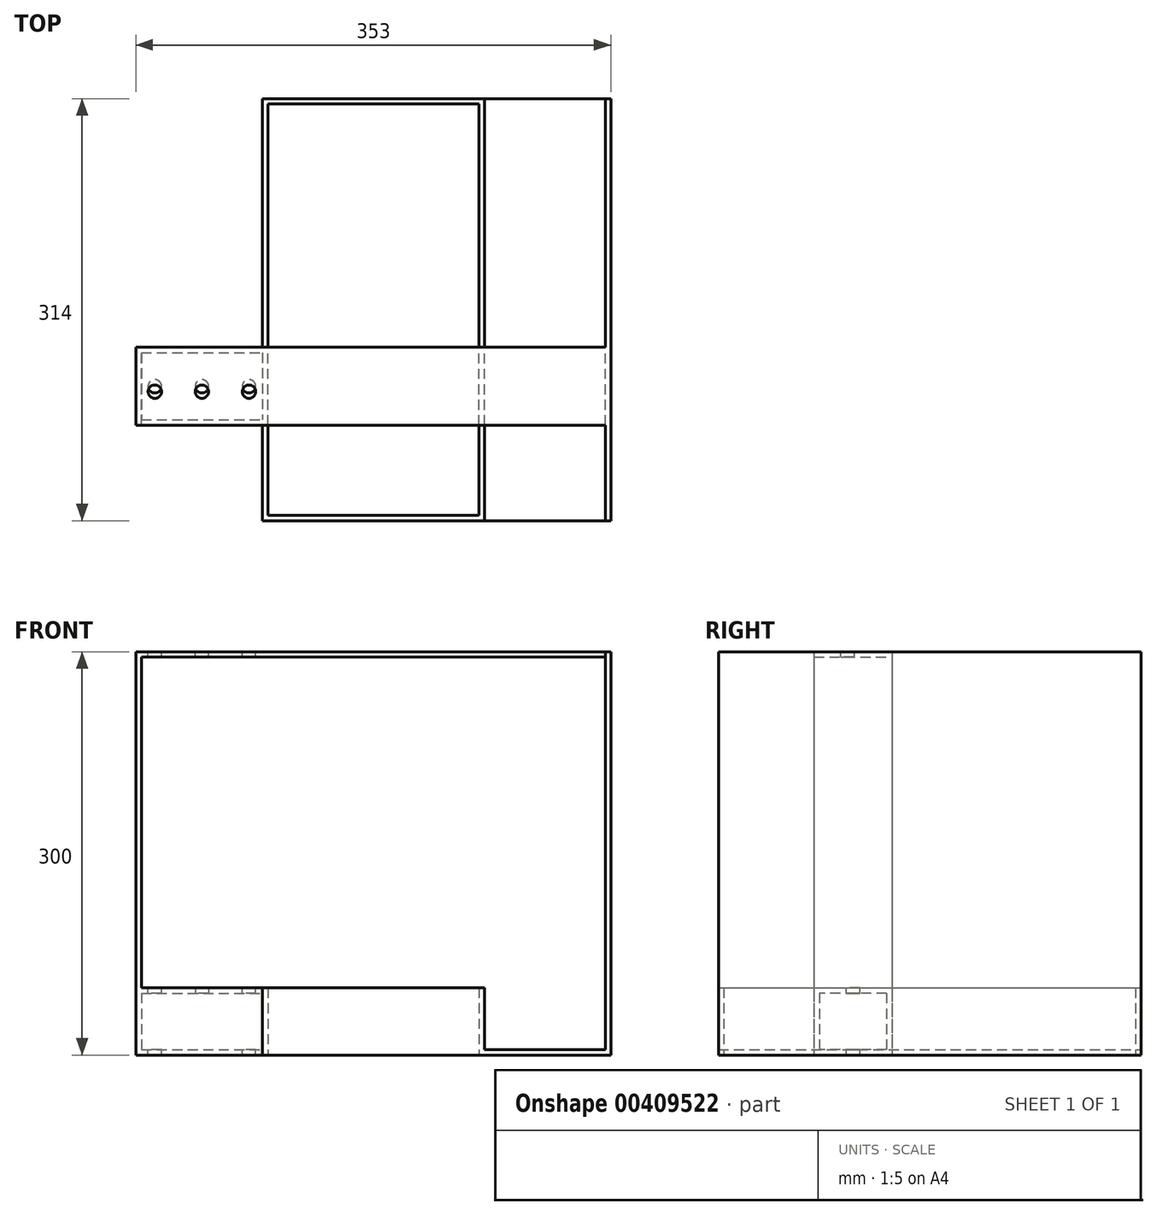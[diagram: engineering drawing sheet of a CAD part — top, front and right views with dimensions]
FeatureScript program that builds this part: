
annotation { "Feature Type Name" : "Feature", "Feature Type Description" : "" }
export const myFeature = defineFeature(function(context is Context, id is Id, definition is map)
    precondition{}
    {
        {
            var Q0;
            Q0=qCreatedBy(makeId("Top.planeOp"),FACE);
            var sketch = newSketch(context, id + "F0", { "sketchPlane" : qUnion([Q0])});
            skLineSegment(sketch, "E0.bottom", {"start": v(-82.5, -165.03) * mm, "end": v(82.5, -165.03) * mm});
            skLineSegment(sketch, "E0.top", {"start": v(-82.5, 148.97) * mm, "end": v(82.5, 148.97) * mm});
            skLineSegment(sketch, "E0.left", {"start": v(-82.5, -165.03) * mm, "end": v(-82.5, 148.97) * mm});
            skLineSegment(sketch, "E0.right", {"start": v(82.5, -165.03) * mm, "end": v(82.5, 148.97) * mm});
            skLineSegment(sketch, "E1.bottom", {"start": v(-78.5, -161.03) * mm, "end": v(78.5, -161.03) * mm});
            skLineSegment(sketch, "E1.top", {"start": v(-78.5, 144.97) * mm, "end": v(78.5, 144.97) * mm});
            skLineSegment(sketch, "E1.left", {"start": v(-78.5, -161.03) * mm, "end": v(-78.5, 144.97) * mm});
            skLineSegment(sketch, "E1.right", {"start": v(78.5, -161.03) * mm, "end": v(78.5, 144.97) * mm});
            skSolve(sketch);
        }
        {
            var Q0;
            Q0=makeQuery(id+"F0.imprint","IMPRINT",FACE,{"disambiguationData":[TD([[makeQuery(id+"F0.imprint","IMPRINT",EDGE,{"derivedFrom":sQuery(id+"F0.wireOp",EDGE,"E0.bottom")}),1.0]])]});
            extrude(context, id + "F1", {"entities" : qUnion([Q0]), "depth" : 50 * mm});
        }
        {
            var Q0;
            Q0=makeQuery(id+"F1.opExtrude","SWEPT_FACE",FACE,{"disambiguationData":[OSD([sQuery(id+"F0.wireOp",EDGE,"E0.left")])]});
            var sketch = newSketch(context, id + "F2", { "sketchPlane" : qUnion([Q0])});
            skLineSegment(sketch, "E2", {"start": v(65.03, 0) * mm, "end": v(65.03, 50) * mm});
            skLineSegment(sketch, "E3.bottom", {"start": v(36.03, 50) * mm, "end": v(94.03, 50) * mm});
            skLineSegment(sketch, "E3.top", {"start": v(36.03, 0) * mm, "end": v(94.03, 0) * mm});
            skLineSegment(sketch, "E3.left", {"start": v(36.03, 50) * mm, "end": v(36.03, 0) * mm});
            skLineSegment(sketch, "E3.right", {"start": v(94.03, 50) * mm, "end": v(94.03, 0) * mm});
            skLineSegment(sketch, "E4.bottom", {"start": v(40.03, 46) * mm, "end": v(90.03, 46) * mm});
            skLineSegment(sketch, "E4.top", {"start": v(40.03, 4) * mm, "end": v(90.03, 4) * mm});
            skLineSegment(sketch, "E4.left", {"start": v(40.03, 46) * mm, "end": v(40.03, 4) * mm});
            skLineSegment(sketch, "E4.right", {"start": v(90.03, 46) * mm, "end": v(90.03, 4) * mm});
            skSolve(sketch);
        }
        {
            var Q0;
            {var subQ3=sQuery(id+"F2.wireOp",EDGE,"E3.left");Q0=makeQuery(id+"F2.imprint","IMPRINT",FACE,{"disambiguationData":[TD([[makeQuery(id+"F2.imprint","IMPRINT",EDGE,{"derivedFrom":subQ3}),1.0]])]});}
            var Q1;
            {var subQ3=sQuery(id+"F2.wireOp",EDGE,"E3.right");Q1=makeQuery(id+"F2.imprint","IMPRINT",FACE,{"disambiguationData":[TD([[makeQuery(id+"F2.imprint","IMPRINT",EDGE,{"derivedFrom":subQ3}),-1.0]])]});}
            extrude(context, id + "F3", {"entities" : qUnion([Q0, Q1]), "operationType" : NewBodyOperationType.ADD, "depth" : 90 * mm});
        }
        {
            var Q0;
            Q0=makeQuery(id+"F3.opExtrude","SWEPT_FACE",FACE,{"disambiguationData":[OSD([sQuery(id+"F2.wireOp",EDGE,"E4.top")])]});
            var sketch = newSketch(context, id + "F4", { "sketchPlane" : qUnion([Q0])});
            skLineSegment(sketch, "E5.bottom", {"start": v(-172.5, 16.97) * mm, "end": v(-150.47, 16.97) * mm});
            skLineSegment(sketch, "E5.top", {"start": v(-172.5, -90.03) * mm, "end": v(-168.5, -90.03) * mm});
            skCircle(sketch, "E6", {"center": v(-92.5, -65.03) * mm, "radius": 5 * mm});
            skCircle(sketch, "E7", {"center": v(-162.5, -65.03) * mm, "radius": 5 * mm});
            skLineSegment(sketch, "E8.bottom", {"start": v(-102.5, -40.03) * mm, "end": v(-152.5, -40.03) * mm});
            skLineSegment(sketch, "E8.top", {"start": v(-102.5, -90.03) * mm, "end": v(-152.5, -90.03) * mm});
            skLineSegment(sketch, "E8.left", {"start": v(-102.5, -40.03) * mm, "end": v(-102.5, -90.03) * mm});
            skLineSegment(sketch, "E8.right", {"start": v(-152.5, -40.03) * mm, "end": v(-152.5, -90.03) * mm});
            skCircle(sketch, "E9", {"center": v(-127.5, -65.03) * mm, "radius": 5 * mm});
            skSolve(sketch);
        }
        {
            var Q0;
            Q0=makeQuery(id+"F4.imprint","IMPRINT",FACE,{"disambiguationData":[TD([[makeQuery(id+"F4.imprint","IMPRINT",EDGE,{"derivedFrom":sQuery(id+"F4.wireOp",EDGE,"E6")}),1.0]])]});
            var Q1;
            Q1=makeQuery(id+"F4.imprint","IMPRINT",FACE,{"disambiguationData":[TD([[makeQuery(id+"F4.imprint","IMPRINT",EDGE,{"derivedFrom":sQuery(id+"F4.wireOp",EDGE,"E7")}),1.0]])]});
            extrude(context, id + "F5", {"entities" : qUnion([Q0, Q1]), "operationType" : NewBodyOperationType.REMOVE, "oppositeDirection" : true, "depth" : 14 * mm, "hasSecondDirection" : true, "secondDirectionOppositeDirection" : false, "secondDirectionDepth" : 70 * mm});
        }
        {
            var Q0;
            Q0=makeQuery(id+"F4.imprint","IMPRINT",FACE,{"disambiguationData":[TD([[makeQuery(id+"F4.imprint","IMPRINT",EDGE,{"derivedFrom":sQuery(id+"F4.wireOp",EDGE,"E9")}),1.0]])]});
            extrude(context, id + "F6", {"entities" : qUnion([Q0]), "operationType" : NewBodyOperationType.REMOVE, "depth" : 50 * mm});
        }
        {
            var Q0;
            Q0=makeQuery(id+"F3.boolean.opBoolean","MERGE",FACE,{"derivedFrom":[makeQuery(id+"F1.opExtrude","CAP_FACE",FACE,{"disambiguationData":[OSD([sQuery(id+"F0.wireOp",EDGE,"E0.bottom"),sQuery(id+"F0.wireOp",EDGE,"E0.top"),sQuery(id+"F0.wireOp",EDGE,"E0.left"),sQuery(id+"F0.wireOp",EDGE,"E0.right"),sQuery(id+"F0.wireOp",EDGE,"E1.bottom"),sQuery(id+"F0.wireOp",EDGE,"E1.top"),sQuery(id+"F0.wireOp",EDGE,"E1.left"),sQuery(id+"F0.wireOp",EDGE,"E1.right")])],"isStart":true}),makeQuery(id+"F3.opExtrude","SWEPT_FACE",FACE,{"disambiguationData":[OSD([sQuery(id+"F2.wireOp",EDGE,"E3.top")])]})]});
            var sketch = newSketch(context, id + "F7", { "sketchPlane" : qUnion([Q0])});
            skLineSegment(sketch, "E10.bottom", {"start": v(-172.5, 36.03) * mm, "end": v(-176.5, 36.03) * mm});
            skLineSegment(sketch, "E10.top", {"start": v(-172.5, 94.03) * mm, "end": v(-176.5, 94.03) * mm});
            skLineSegment(sketch, "E10.left", {"start": v(-172.5, 36.03) * mm, "end": v(-172.5, 94.03) * mm});
            skLineSegment(sketch, "E10.right", {"start": v(-176.5, 36.03) * mm, "end": v(-176.5, 94.03) * mm});
            skSolve(sketch);
        }
        {
            var Q0;
            Q0 = qSketchRegion(id + "F7", true);
            extrude(context, id + "F8", {"entities" : qUnion([Q0]), "operationType" : NewBodyOperationType.ADD, "oppositeDirection" : true, "depth" : 300 * mm});
        }
        {
            var Q0;
            {var subQ1=sQuery(id+"F7.wireOp",EDGE,"E10.left");Q0=makeQuery(id+"F8.boolean.opBoolean","SPLIT",FACE,{"disambiguationData":[TD([makeQuery(id+"F3.opExtrude","SWEPT_FACE",FACE,{"disambiguationData":[OSD([sQuery(id+"F2.wireOp",EDGE,"E3.bottom")])]})])],"derivedFrom":makeQuery(id+"F8.opExtrude","SWEPT_FACE",FACE,{"disambiguationData":[OSD([subQ1])]})});}
            var sketch = newSketch(context, id + "F9", { "sketchPlane" : qUnion([Q0])});
            skLineSegment(sketch, "E11.bottom", {"start": v(-94.03, 300) * mm, "end": v(-36.03, 300) * mm});
            skLineSegment(sketch, "E11.top", {"start": v(-94.03, 296) * mm, "end": v(-36.03, 296) * mm});
            skLineSegment(sketch, "E11.left", {"start": v(-94.03, 300) * mm, "end": v(-94.03, 296) * mm});
            skLineSegment(sketch, "E11.right", {"start": v(-36.03, 300) * mm, "end": v(-36.03, 296) * mm});
            skSolve(sketch);
        }
        {
            var Q0;
            Q0 = qSketchRegion(id + "F9", true);
            var Q1;
            Q1 = qSketchRegion(id + "F11", true);
            extrude(context, id + "F10", {"entities" : qUnion([Q0, Q1]), "operationType" : NewBodyOperationType.ADD, "depth" : 345 * mm});
        }
        {
            var Q0;
            Q0=makeQuery(id+"F1.opExtrude","SWEPT_FACE",FACE,{"disambiguationData":[OSD([sQuery(id+"F0.wireOp",EDGE,"E0.right")])]});
            var sketch = newSketch(context, id + "F11", { "sketchPlane" : qUnion([Q0])});
            skLineSegment(sketch, "E12.bottom", {"start": v(-165.03, 0) * mm, "end": v(148.97, 0) * mm});
            skLineSegment(sketch, "E12.top", {"start": v(-165.03, 4) * mm, "end": v(148.97, 4) * mm});
            skLineSegment(sketch, "E12.left", {"start": v(-165.03, 0) * mm, "end": v(-165.03, 4) * mm});
            skLineSegment(sketch, "E12.right", {"start": v(148.97, 0) * mm, "end": v(148.97, 4) * mm});
            skSolve(sketch);
        }
        {
            var Q0;
            Q0 = qSketchRegion(id + "F11", true);
            extrude(context, id + "F12", {"entities" : qUnion([Q0]), "operationType" : NewBodyOperationType.ADD, "depth" : 90 * mm});
        }
        {
            var Q0;
            Q0=makeQuery(id+"F12.boolean.opBoolean","MERGE",FACE,{"derivedFrom":[makeQuery(id+"F8.boolean.opBoolean","MERGE",FACE,{"derivedFrom":[makeQuery(id+"F3.boolean.opBoolean","MERGE",FACE,{"derivedFrom":[makeQuery(id+"F1.opExtrude","CAP_FACE",FACE,{"disambiguationData":[OSD([sQuery(id+"F0.wireOp",EDGE,"E0.bottom"),sQuery(id+"F0.wireOp",EDGE,"E0.top"),sQuery(id+"F0.wireOp",EDGE,"E0.left"),sQuery(id+"F0.wireOp",EDGE,"E0.right"),sQuery(id+"F0.wireOp",EDGE,"E1.bottom"),sQuery(id+"F0.wireOp",EDGE,"E1.top"),sQuery(id+"F0.wireOp",EDGE,"E1.left"),sQuery(id+"F0.wireOp",EDGE,"E1.right")])],"isStart":true}),makeQuery(id+"F3.opExtrude","SWEPT_FACE",FACE,{"disambiguationData":[OSD([sQuery(id+"F2.wireOp",EDGE,"E3.top")])]})]}),makeQuery(id+"F8.opExtrude","CAP_FACE",FACE,{"disambiguationData":[OSD([sQuery(id+"F7.wireOp",EDGE,"E10.bottom"),sQuery(id+"F7.wireOp",EDGE,"E10.top"),sQuery(id+"F7.wireOp",EDGE,"E10.left"),sQuery(id+"F7.wireOp",EDGE,"E10.right")])],"isStart":true})]}),makeQuery(id+"F12.opExtrude","SWEPT_FACE",FACE,{"disambiguationData":[OSD([sQuery(id+"F11.wireOp",EDGE,"E12.bottom")])]})]});
            var sketch = newSketch(context, id + "F13", { "sketchPlane" : qUnion([Q0])});
            skLineSegment(sketch, "E13.bottom", {"start": v(172.5, 165.03) * mm, "end": v(176.5, 165.03) * mm});
            skLineSegment(sketch, "E13.top", {"start": v(172.5, -148.97) * mm, "end": v(176.5, -148.97) * mm});
            skLineSegment(sketch, "E13.left", {"start": v(172.5, 165.03) * mm, "end": v(172.5, -148.97) * mm});
            skLineSegment(sketch, "E13.right", {"start": v(176.5, 165.03) * mm, "end": v(176.5, -148.97) * mm});
            skSolve(sketch);
        }
        {
            var Q0;
            Q0 = qSketchRegion(id + "F13", true);
            extrude(context, id + "F14", {"entities" : qUnion([Q0]), "operationType" : NewBodyOperationType.ADD, "oppositeDirection" : true, "depth" : 300 * mm});
        }
        {
            var Q0;
            Q0=makeQuery(id+"F14.boolean.opBoolean","MERGE",FACE,{"derivedFrom":[makeQuery(id+"F10.boolean.opBoolean","MERGE",FACE,{"derivedFrom":[makeQuery(id+"F8.opExtrude","CAP_FACE",FACE,{"disambiguationData":[OSD([sQuery(id+"F7.wireOp",EDGE,"E10.bottom"),sQuery(id+"F7.wireOp",EDGE,"E10.top"),sQuery(id+"F7.wireOp",EDGE,"E10.left"),sQuery(id+"F7.wireOp",EDGE,"E10.right")])],"isStart":false}),makeQuery(id+"F10.opExtrude","SWEPT_FACE",FACE,{"disambiguationData":[OSD([sQuery(id+"F9.wireOp",EDGE,"E11.bottom")])]})]}),makeQuery(id+"F14.opExtrude","CAP_FACE",FACE,{"disambiguationData":[OSD([sQuery(id+"F13.wireOp",EDGE,"E13.bottom"),sQuery(id+"F13.wireOp",EDGE,"E13.top"),sQuery(id+"F13.wireOp",EDGE,"E13.left"),sQuery(id+"F13.wireOp",EDGE,"E13.right")])],"isStart":false})]});
            var sketch = newSketch(context, id + "F15", { "sketchPlane" : qUnion([Q0])});
            skCircle(sketch, "E14", {"center": v(-92.5, -69.03) * mm, "radius": 5 * mm});
            skCircle(sketch, "E15", {"center": v(-127.5, -69.03) * mm, "radius": 5 * mm});
            skCircle(sketch, "E16", {"center": v(-162.5, -69.03) * mm, "radius": 5 * mm});
            skSolve(sketch);
        }
        {
            var Q0;
            Q0 = qSketchRegion(id + "F15", true);
            extrude(context, id + "F16", {"entities" : qUnion([Q0]), "operationType" : NewBodyOperationType.REMOVE, "oppositeDirection" : true, "depth" : 29 * mm});
        }
    });
